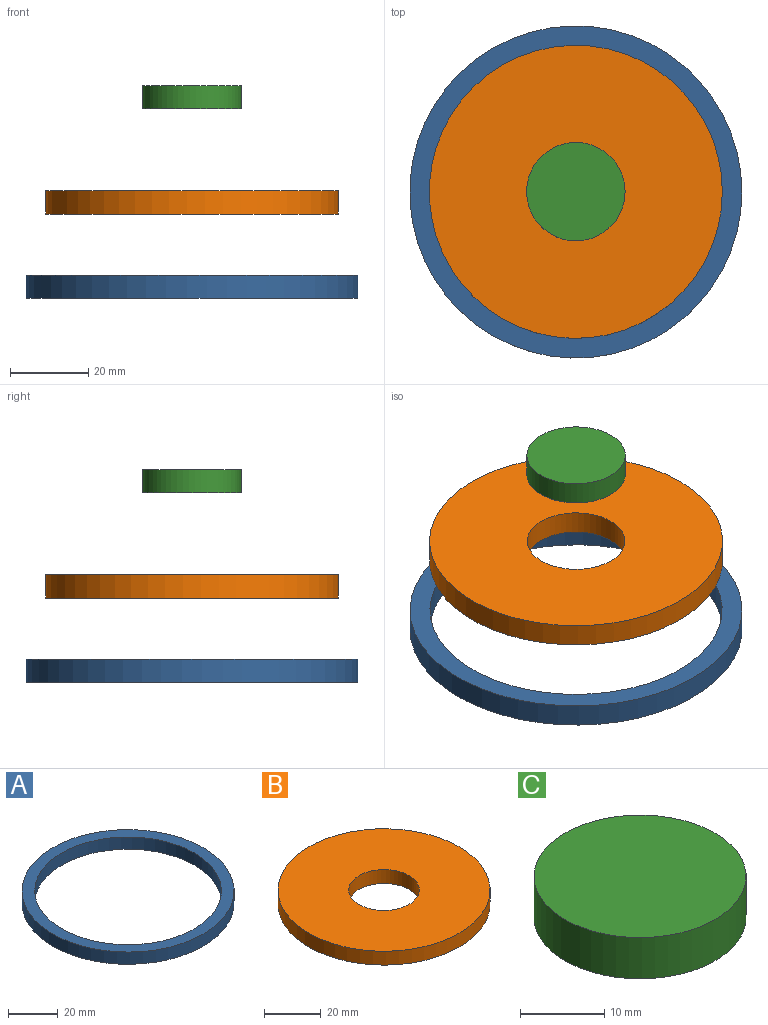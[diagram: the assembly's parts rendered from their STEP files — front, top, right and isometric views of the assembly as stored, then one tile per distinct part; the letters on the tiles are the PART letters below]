
ASSEMBLY  parts=3 mates=2
PART A: 4 faces, bbox 85x85x6 mm
  f0: cylinder r=37.4mm len=74.8mm, axis (0,0,-1), area 1409.9mm2, adj f2,f3
  f1: cylinder r=42.5mm len=85mm, axis (0,0,-1), area 1602.2mm2, adj f2,f3
  f2: plane 85x85mm, normal (0,0,1), area 1280.2mm2, adj f0,f1
  f3: plane 85x85mm, normal (0,0,-1), area 1280.2mm2, adj f0,f1
PART B: 4 faces, bbox 75x75x6 mm
  f0: cylinder r=37.5mm len=75mm, axis (0,0,-1), area 1413.7mm2, adj f1,f2
  f1: plane 75x75mm, normal (0,0,1), area 3927mm2, adj f0,f3
  f2: plane 75x75mm, normal (0,0,-1), area 3927mm2, adj f0,f3
  f3: cylinder r=12.5mm len=25mm, axis (0,0,1), area 471.2mm2, adj f1,f2
PART C: 3 faces, bbox 25.2x25.2x6 mm
  f0: cylinder r=12.6mm len=25.2mm, axis (0,0,-1), area 475mm2, adj f1,f2
  f1: plane 25.2x25.2mm, normal (0,0,1), area 498.8mm2, adj f0
  f2: plane 25.2x25.2mm, normal (0,0,-1), area 498.8mm2, adj f0
PLACE A t=(-26.5,-7.47,-4.41)mm
PLACE B t=(-26.5,-7.47,17.19)mm
PLACE C t=(-26.5,-7.47,44.07)mm
MATE cylindrical B.f0 <-> A.f0  axis (0,0,-1) through (-26.5,-7.47,17.19)mm
MATE cylindrical C.f0 <-> B.f3  axis (0,0,-1) through (-26.5,-7.47,44.07)mm
